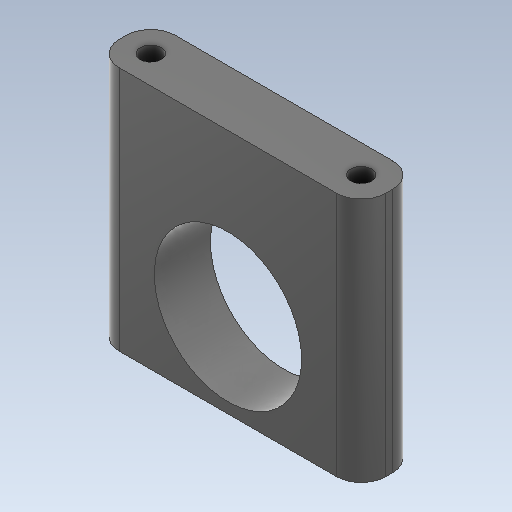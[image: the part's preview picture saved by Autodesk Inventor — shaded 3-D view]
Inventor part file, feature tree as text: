
AUTODESK INVENTOR PART (.ipt)
format: ipt  version: 2020 (Build 240168000, 168)  size: 156,672 bytes
history: native  units: mm
features: projected_geometry x6, sketch x3, extrude x2, other x1, fillet x1
ambient origin geometry x8: Origin, YZ Plane, XZ Plane, XY Plane, X Axis, Y Axis, Z Axis, Center Point
bodies: Body1 (feature_tree)
feature tree (13):
  other  "Твердое тело1"
  sketch  "Эскиз1"
  extrude  "Выдавливание1"  Depth=30.0mm
  fillet  "Сопряжение1"  Radius=3.0mm
  extrude  "Выдавливание2"  Depth=38.0mm
  sketch  "Эскиз2"
  sketch  "Эскиз3"
  projected_geometry  "Спроецированная петля1"
  projected_geometry  "Спроецированная петля2"
  projected_geometry  "Спроецированная петля3"
  projected_geometry  "Спроецированная петля4"
  projected_geometry  "Спроецированная петля5"
  projected_geometry  "Спроецированная петля6"
